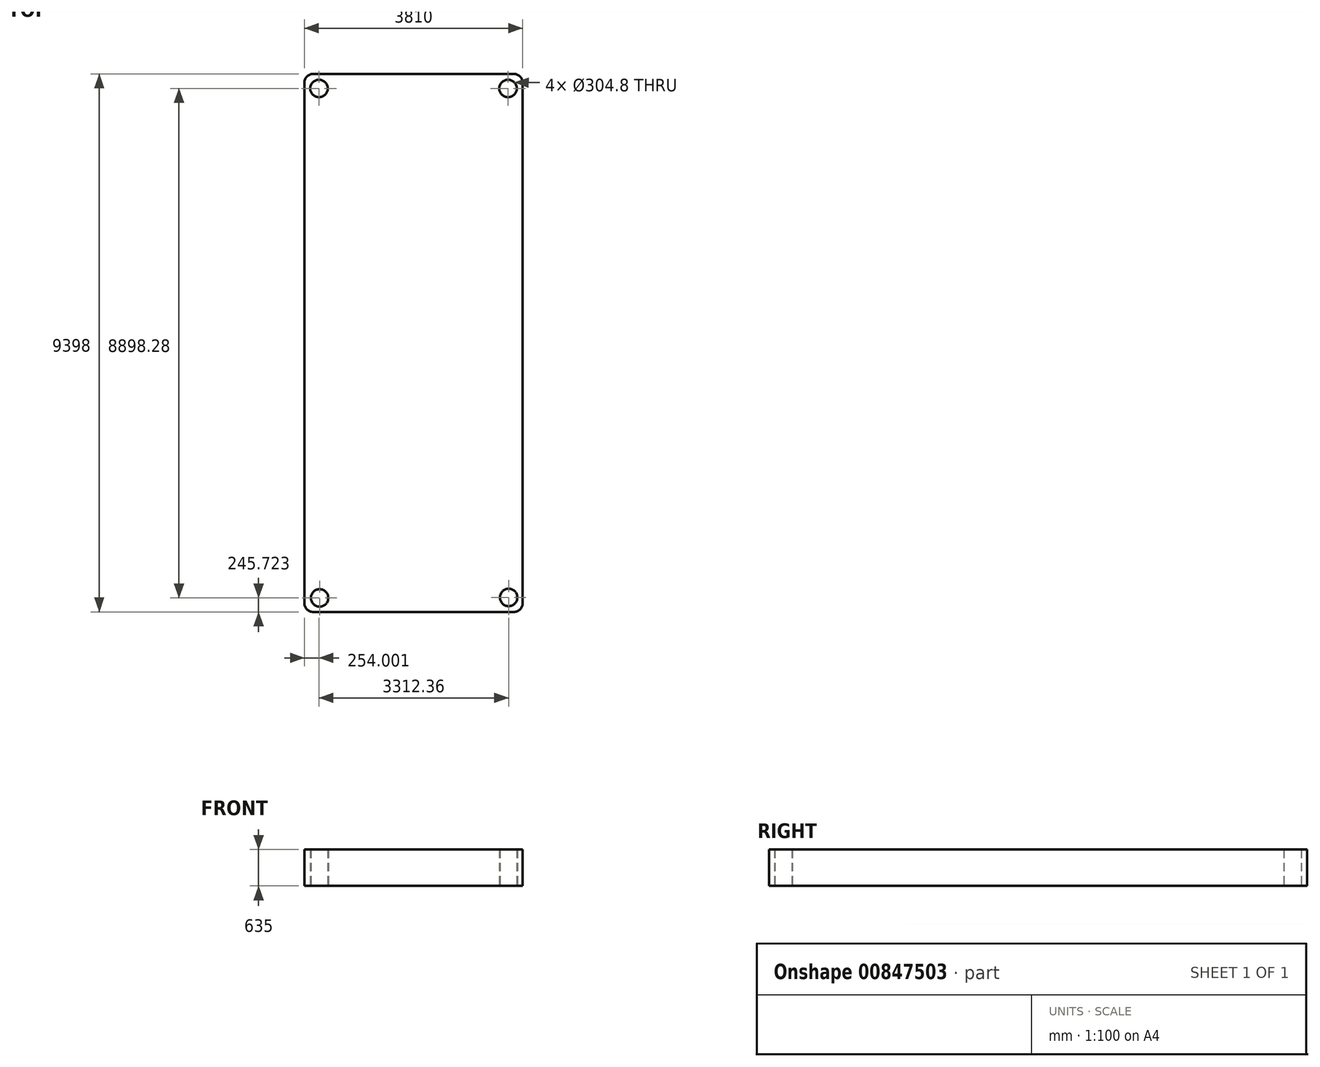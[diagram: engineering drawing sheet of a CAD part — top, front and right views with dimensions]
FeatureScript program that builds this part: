
annotation { "Feature Type Name" : "Feature", "Feature Type Description" : "" }
export const myFeature = defineFeature(function(context is Context, id is Id, definition is map)
    precondition{}
    {
        {
            var Q0;
            Q0=qCreatedBy(makeId("Top.planeOp"),FACE);
            var sketch = newSketch(context, id + "F0", { "sketchPlane" : qUnion([Q0])});
            skLineSegment(sketch, "E0.bottom", {"start": v(-2155.42, -4694.56) * mm, "end": v(1654.58, -4694.56) * mm});
            skLineSegment(sketch, "E0.top", {"start": v(-2155.42, 4703.44) * mm, "end": v(1654.58, 4703.44) * mm});
            skLineSegment(sketch, "E0.left", {"start": v(-2155.42, -4694.56) * mm, "end": v(-2155.42, 4703.44) * mm});
            skLineSegment(sketch, "E0.right", {"start": v(1654.58, -4694.56) * mm, "end": v(1654.58, 4703.44) * mm});
            skCircle(sketch, "E1", {"center": v(-1901.42, 4449.44) * mm, "radius": 152.4 * mm});
            skLineSegment(sketch, "E2", {"start": v(-250.42, 4703.44) * mm, "end": v(-250.42, -4694.56) * mm, "construction": true});
            skLineSegment(sketch, "E3", {"start": v(1654.58, 4.44) * mm, "end": v(-2155.42, 0) * mm, "construction": true});
            skPoint(sketch, "E3.endSnap0", {"position": v(-2155.42, 4.44) * mm});
            skCircle(sketch, "E4.MirrorC", {"center": v(1400.58, 4449.44) * mm, "radius": 152.4 * mm});
            skCircle(sketch, "E5.MirrorC", {"center": v(1410.94, -4441.14) * mm, "radius": 152.4 * mm});
            skCircle(sketch, "E6.MirrorC", {"center": v(-1891.05, -4448.84) * mm, "radius": 152.4 * mm});
            skSolve(sketch);
        }
        {
            var Q0;
            Q0=makeQuery(id+"F0.imprint","IMPRINT",FACE,{"disambiguationData":[TD([[makeQuery(id+"F0.imprint","IMPRINT",EDGE,{"derivedFrom":sQuery(id+"F0.wireOp",EDGE,"E0.bottom")}),1.0]])]});
            extrude(context, id + "F1", {"entities" : qUnion([Q0]), "depth" : 635 * mm, "offsetDistance" : 25.4 * mm});
        }
        {
            var Q0;
            Q0=makeQuery(id+"F1.opExtrude","SWEPT_EDGE",EDGE,{"disambiguationData":[OSD([sQuery(id+"F0.wireOp",EDGE,"E0.top"),sQuery(id+"F0.wireOp",EDGE,"E0.right")])]});
            var Q1;
            Q1=makeQuery(id+"F1.opExtrude","SWEPT_EDGE",EDGE,{"disambiguationData":[OSD([sQuery(id+"F0.wireOp",EDGE,"E0.top"),sQuery(id+"F0.wireOp",EDGE,"E0.left")])]});
            var Q2;
            Q2=makeQuery(id+"F1.opExtrude","SWEPT_EDGE",EDGE,{"disambiguationData":[OSD([sQuery(id+"F0.wireOp",EDGE,"E0.bottom"),sQuery(id+"F0.wireOp",EDGE,"E0.left")])]});
            var Q3;
            Q3=makeQuery(id+"F1.opExtrude","SWEPT_EDGE",EDGE,{"disambiguationData":[OSD([sQuery(id+"F0.wireOp",EDGE,"E0.bottom"),sQuery(id+"F0.wireOp",EDGE,"E0.right")])]});
            fillet(context, id + "F2", {"entities" : qUnion([Q0, Q1, Q2, Q3]), "radius" : 152.4 * mm, "tangentPropagation" : true, "allowEdgeOverflow" : false});
        }
    });
